FCSTD DOCUMENT  (FreeCAD 0.22R35720 (Git))
Label: DigitalTwin
License: All rights reserved
LicenseURL: http://en.wikipedia.org/wiki/All_rights_reserved
objects: Part::Feature×86, App::FeaturePython×76, App::Part×61, Part::FeaturePython×47, App::DocumentObjectGroup×4, Spreadsheet::Sheet×2
note: 132 computed .brp shape members not serialized (recipe doc carries the construction recipe); baked Part::Feature solids carry a one-line shape summary decoded from their .brp

FEATURE [Spreadsheet::Sheet] Spreadsheet  label="Offsets"
  cells = C3='Offsets; D4='R1; H4='R2; C5='Axis; D5='Y; E5='Z; F5='C; H5='Y; I5='Z; J5='C; C6='x; D6(R1_Y_x)=-404.5; E6(R1_Z_x)=-405; F6(R1_C_x)=-307.3; H6(R2_Y_x)=404.5; I6(R2_Z_x)=405; J6(R2_C_x)=307.3; C7='y; D7(R1_Y_y)=-285.5; E7(R1_Z_y)=-84.5; F7(R1_C_y)=-137.5; H7(R2_Y_y)=286.5; I7(R2_Z_y)=85.5; J7(R2_C_y)=138.5; C8='z; D8(R1_Y_z)=157; E8(R1_Z_z)=43; F8(R1_C_z)=207; H8(R2_Y_z)=157; I8(R2_Z_z)=43; J8(R2_C_z)=207; C9='Rot; C10='x; D10(R1_Y_rotX)=0; E10(R1_Z_rotX)=1; F10(R1_C_rotX)=0.58; H10(R2_Y_rotX)=0; I10(R2_Z_rotX)=0; J10(R2_C_rotX)=-0.58; C11='y; D11(R1_Y_rotY)=0; E11(R1_Z_rotY)=0; F11(R1_C_rotY)=0.58; H11(R2_Y_rotY)=0; I11(R2_Z_rotY)=0.71; J11(R2_C_rotY)=0.58; C12='z; D12(R1_Y_rotZ)=1; E12(R1_Z_rotZ)=0; F12(R1_C_rotZ)=-0.58; H12(R2_Y_rotZ)=-1; I12(R2_Z_rotZ)=0.71; J12(R2_C_rotZ)=-0.58; C13='a; D13(R1_Y_rotA)=90; E13(R1_Z_rotA)=90; F13(R1_C_rotA)=240; H13(R2_Y_rotA)=90; I13(R2_Z_rotA)=180; J13(R2_C_rotA)=120
FEATURE [Part::Feature] Part__Feature  label="SOLID"
  shape: bbox 125.9 x 42 x 74 mm, 165 faces (baked)
FEATURE [App::Part] Cartesian1_XYCarriage
  Group = -> [Part__Feature]
  Origin = -> Origin
  Placement = pos=(0,0,0) rot=(0.57735,0.57735,-0.57735;4.18879rad)
FEATURE [Part::Feature] Part__Feature002  label="SOLID001"
  shape: bbox 40 x 48 x 60 mm, 15 faces (baked)
FEATURE [App::Part] Cartesian1_BallNut
  Group = -> [Part__Feature002]
  Origin = -> Origin001
  Placement = pos=(-70,50,-1.84331e-08) rot=(0.707107,0,0.707107;3.14159rad)
FEATURE [App::Part] Carriage  label="C"
  Group = -> [Cartesian1_XYCarriage,Cartesian1_BallNut]
  Origin = -> Origin002
FEATURE [Part::Feature] Part__Feature028  label="SOLID002"
  shape: bbox 45 x 70.5 x 201 mm, 88 faces (baked)
FEATURE [App::Part] XMotorMount
  Group = -> [Part__Feature028]
  Origin = -> Origin003
  Placement = pos=(0,40,-6.39e-14) rot=(0,1,0;3.14159rad)
FEATURE [Part::Feature] Part__Feature030  label="SOLID003"
  shape: bbox 750 x 50 x 14 mm, 23 faces (baked)
FEATURE [App::Part] WS_10_40_X
  Group = -> [Part__Feature030]
  Origin = -> Origin004
  Placement = pos=(-45,20.5,69) rot=(0,0,1;0rad)
FEATURE [Part::Feature] Part__Feature032  label="SOLID004"
  shape: bbox 750 x 50 x 14 mm, 23 faces (baked)
FEATURE [App::Part] WS_10_40_X001
  Group = -> [Part__Feature032]
  Origin = -> Origin005
  Placement = pos=(-45,59.5,-69) rot=(1,0,0;3.14159rad)
FEATURE [Part::Feature] Part__Feature034  label="SOLID005"
  shape: bbox 45 x 70.5 x 201 mm, 82 faces (baked)
FEATURE [App::Part] XFloating
  Group = -> [Part__Feature034]
  Origin = -> Origin006
  Placement = pos=(512.817,40,-1.012e-13) rot=(0,0,1;0rad)
FEATURE [Part::Feature] Part__Feature036  label="Nema17 Stepper Motor"
  Placement = pos=(-85.5,39.998,-0.00196609) rot=(0,0,-1;1.5708rad)
  shape: bbox 64.02 x 42.26 x 48.39 mm, 313 faces (baked)
FEATURE [Part::Feature] Part__Feature037  label="SOLID006"
  shape: bbox 18.95 x 18.95 x 539 mm, 68 faces (baked)
FEATURE [App::Part] Cartesian1_BallScrew
  Group = -> [Part__Feature037]
  Origin = -> Origin007
  Placement = pos=(-9,40,-6.16e-14) rot=(0.64284,0.416548,0.64284;2.35221rad)
FEATURE [Part::Feature] Part__Feature039  label="SOLID007"
  shape: bbox 37 x 37 x 7 mm, 8 faces (baked)
FEATURE [App::Part] Cartesian2_BallBearing_25x37x7
  Group = -> [Part__Feature039]
  Origin = -> Origin008
  Placement = pos=(512.817,40,-1.012e-13) rot=(0.309507,0.899117,0.309507;1.67694rad)
FEATURE [Part::Feature] Part__Feature041  label="SOLID008"
  shape: bbox 25 x 25 x 32 mm, 12 faces (baked)
FEATURE [App::Part] Cartesian1_12_12_Clutch
  Group = -> [Part__Feature041]
  Origin = -> Origin009
  Placement = pos=(-31,40,-6.39e-14) rot=(0.684544,0.2506,0.684544;2.65051rad)
FEATURE [Part::Feature] Part__Feature043  label="SOLID009"
  shape: bbox 30 x 17 x 30 mm, 8 faces (baked)
FEATURE [App::Part] endCup
  Group = -> [Part__Feature043]
  Origin = -> Origin010
  Placement = pos=(512.817,40,-1.012e-13) rot=(0.652231,0.652231,-0.386251;2.4044rad)
FEATURE [Part::Feature] Part__Feature045  label="SOLID010"
  shape: bbox 8 x 18.5 x 18.2 mm, 16 faces (baked)
FEATURE [App::Part] Connector_female
  Group = -> [Part__Feature045]
  Origin = -> Origin011
  Placement = pos=(-32.15,60,39.85) rot=(0,-1,0;1.5708rad)
FEATURE [Part::Feature] Part__Feature047  label="SOLID011"
  shape: bbox 6.5 x 11 x 20 mm, 8 faces (baked)
FEATURE [App::Part] stopSw
  Group = -> [Part__Feature047]
  Origin = -> Origin012
  Placement = pos=(517.817,59,-40) rot=(0.707107,-0.707107,0;3.14159rad)
FEATURE [App::Part] X
  Group = -> [XMotorMount,WS_10_40_X,WS_10_40_X001,XFloating,Part__Feature036,Cartesian1_BallScrew,Cartesian2_BallBearing_25x37x7,Cartesian1_12_12_Clutch,endCup,Connector_female,stopSw]
  Origin = -> Origin013
FEATURE [Part::Feature] Part__Feature169  label="SOLID012"
  shape: bbox 74 x 74 x 26.9 mm, 46 faces (baked)
FEATURE [App::Part] YItemEnd
  Group = -> [Part__Feature169]
  Origin = -> Origin014
  Placement = pos=(0,0,7.1e-15) rot=(-1,0,0;1.5708rad)
FEATURE [Part::Feature] Part__Feature171  label="SOLID013"
  shape: bbox 74 x 100 x 44 mm, 108 faces (baked)
FEATURE [App::Part] YRodMount
  Group = -> [Part__Feature171]
  Origin = -> Origin015
  Placement = pos=(3.91e-14,-2,-74) rot=(1,0,0;1.5708rad)
FEATURE [Part::Feature] Part__Feature173  label="SOLID014"
  shape: bbox 69 x 75 x 42 mm, 58 faces (baked)
FEATURE [App::Part] YMotorMount
  Group = -> [Part__Feature173]
  Origin = -> Origin016
  Placement = pos=(2.41e-14,-6,-74) rot=(1,0,0;1.5708rad)
FEATURE [Part::Feature] Part__Feature175  label="SOLID015"
  shape: bbox 11 x 75 x 5 mm, 15 faces (baked)
FEATURE [App::Part] YEndStopMount
  Group = -> [Part__Feature175]
  Origin = -> Origin017
  Placement = pos=(64.39,-10,-37) rot=(1,0,0;1.5708rad)
FEATURE [Part::Feature] Part__Feature177  label="SOLID016"
  shape: bbox 6.5 x 11 x 20 mm, 8 faces (baked)
FEATURE [App::Part] stopSw001
  Group = -> [Part__Feature177]
  Origin = -> Origin018
  Placement = pos=(68.64,-15,-56.5) rot=(0,0,-1;1.5708rad)
FEATURE [App::Part] YSub1
  Group = -> [YItemEnd,YRodMount,YMotorMount,YEndStopMount,stopSw001]
  Origin = -> Origin019
  Placement = pos=(5.6488e-12,-70.2,36.5) rot=(0,0,1;0rad)
FEATURE [Part::Feature] Part__Feature179  label="SOLID017"
  shape: bbox 74 x 75 x 43.5 mm, 64 faces (baked)
FEATURE [App::Part] YFloatingMount
  Group = -> [Part__Feature179]
  Origin = -> Origin020
  Placement = pos=(11.243,57.3809,-132.972) rot=(0,0,1;0rad)
FEATURE [Part::Feature] Part__Feature181  label="SOLID018"
  shape: bbox 74 x 100 x 44 mm, 108 faces (baked)
FEATURE [App::Part] YRodMount001
  Group = -> [Part__Feature181]
  Origin = -> Origin021
  Placement = pos=(11.243,57.3809,-136.972) rot=(0,0,1;0rad)
FEATURE [App::Part] YSub2
  Group = -> [YFloatingMount,YRodMount001]
  Origin = -> Origin022
  Placement = pos=(486.757,-209.172,-94.3809) rot=(1,0,0;1.5708rad)
FEATURE [Part::Feature] Part__Feature183  label="SOLID019"
  shape: bbox 74 x 74 x 26.9 mm, 46 faces (baked)
FEATURE [App::Part] YItemEnd001
  Group = -> [Part__Feature183]
  Origin = -> Origin023
  Placement = pos=(572,-70.2,-37.5) rot=(0,0.707107,0.707107;3.14159rad)
FEATURE [Part::Feature] Part__Feature185  label="item_0037003_Profile_5_20x20_L=564_1"
  Placement = pos=(286,-55,-16.5) rot=(0,0,1;1.5708rad)
  shape: bbox 564 x 20 x 20 mm, 75 faces (baked)
FEATURE [Part::Feature] Part__Feature186  label="item_0037003_Profile_5_20x20_L=564_002"
  Placement = pos=(286,-55,15.5) rot=(0,0,1;1.5708rad)
  shape: bbox 564 x 20 x 20 mm, 75 faces (baked)
FEATURE [Part::Feature] Part__Feature187  label="SOLID020"
  shape: bbox 12 x 12 x 564 mm, 5 faces (baked)
FEATURE [App::Part] Cartesian1_12mm_Rod
  Group = -> [Part__Feature187]
  Origin = -> Origin024
  Placement = pos=(4,-97.2,-50.5) rot=(-0.52942,0.662894,-0.52942;1.97082rad)
FEATURE [Part::Feature] Part__Feature189  label="SOLID021"
  shape: bbox 12 x 12 x 564 mm, 5 faces (baked)
FEATURE [App::Part] Cartesian1_12mm_Rod001
  Group = -> [Part__Feature189]
  Origin = -> Origin025
  Placement = pos=(4,-97.2,50) rot=(0.611639,0.501791,0.611639;2.21143rad)
FEATURE [Part::Feature] Part__Feature191  label="SOLID022"
  shape: bbox 37 x 37 x 7 mm, 8 faces (baked)
FEATURE [App::Part] Cartesian2_BallBearing_25x37x7001
  Group = -> [Part__Feature191]
  Origin = -> Origin026
  Placement = pos=(564,-97.2,-1.37e-14) rot=(0.634829,0.440435,0.634829;2.31185rad)
FEATURE [Part::Feature] Part__Feature193  label="SOLID023"
  shape: bbox 34 x 9 x 45 mm, 26 faces (baked)
FEATURE [App::Part] Cartesian1_X_RodCover
  Group = -> [Part__Feature193]
  Origin = -> Origin027
  Placement = pos=(573.8,-97.2,-50) rot=(-0.57735,-0.57735,0.57735;2.0944rad)
FEATURE [Part::Feature] Part__Feature195  label="SOLID024"
  shape: bbox 34 x 9 x 45 mm, 26 faces (baked)
FEATURE [App::Part] Cartesian1_X_RodCover001
  Group = -> [Part__Feature195]
  Origin = -> Origin028
  Placement = pos=(573.8,-97.2,50) rot=(0.57735,-0.57735,-0.57735;2.0944rad)
FEATURE [Part::Feature] Part__Feature197  label="SOLID025"
  shape: bbox 34 x 9 x 45 mm, 26 faces (baked)
FEATURE [App::Part] Cartesian1_X_RodCover002
  Group = -> [Part__Feature197]
  Origin = -> Origin029
  Placement = pos=(24,-97.2,49.5) rot=(0.57735,0.57735,0.57735;2.0944rad)
FEATURE [Part::Feature] Part__Feature199  label="SOLID026"
  shape: bbox 34 x 9 x 45 mm, 26 faces (baked)
FEATURE [App::Part] Cartesian1_X_RodCover003
  Group = -> [Part__Feature199]
  Origin = -> Origin030
  Placement = pos=(24,-97.2,-50.5) rot=(0.57735,-0.57735,0.57735;4.18879rad)
FEATURE [Part::Feature] Part__Feature201  label="Nema17 Stepper Motor001"
  Placement = pos=(-40.5,-97.2,-5.58e-13) rot=(-0.57735,-0.57735,-0.57735;2.0944rad)
  shape: bbox 64.02 x 48.39 x 42.26 mm, 313 faces (baked)
FEATURE [Part::Feature] Part__Feature202  label="SOLID027"
  shape: bbox 25 x 25 x 32 mm, 12 faces (baked)
FEATURE [App::Part] Cartesian1_12_12_Clutch001
  Group = -> [Part__Feature202]
  Origin = -> Origin031
  Placement = pos=(7.85,-97.2,-5.127e-13) rot=(0.704181,-0.09087,0.704181;3.32283rad)
FEATURE [Part::Feature] Part__Feature204  label="SOLID028"
  shape: bbox 18.95 x 18.95 x 539 mm, 68 faces (baked)
FEATURE [App::Part] Cartesian1_BallScrew001
  Group = -> [Part__Feature204]
  Origin = -> Origin032
  Placement = pos=(29.85,-97.2,-4.874e-13) rot=(0.707075,-0.00955,0.707075;3.16069rad)
FEATURE [Part::Feature] Part__Feature206  label="SOLID029"
  shape: bbox 18 x 74 x 74 mm, 62 faces (baked)
FEATURE [App::Part] YItemEndCover
  Group = -> [Part__Feature206]
  Origin = -> Origin033
  Placement = pos=(535,-45.2,-0.5) rot=(0.57735,0.57735,0.57735;2.0944rad)
FEATURE [Part::Feature] Part__Feature208  label="SOLID030"
  shape: bbox 48 x 100 x 73 mm, 95 faces (baked)
FEATURE [App::Part] YCarriage
  Group = -> [Part__Feature208]
  Origin = -> Origin034
  Placement = pos=(201,0,-0.5) rot=(-0.57735,0.57735,0.57735;4.18879rad)
FEATURE [Part::Feature] Part__Feature210  label="SOLID031"
  shape: bbox 48 x 48 x 35 mm, 12 faces (baked)
FEATURE [App::Part] YCarriageNut
  Group = -> [Part__Feature210]
  Origin = -> Origin035
  Placement = pos=(201,-21,31.5) rot=(0,0,1;3.66519rad)
FEATURE [Part::Feature] Part__Feature212  label="WJ200UM_01_10_1"
  Placement = pos=(181,9,20.5) rot=(1,0,0;1.5708rad)
  shape: bbox 26 x 16.5 x 29 mm, 220 faces (baked)
FEATURE [Part::Feature] Part__Feature213  label="WJ200UM_01_10_002"
  Placement = pos=(181,9,-50.5) rot=(1,0,0;1.5708rad)
  shape: bbox 26 x 16.5 x 29 mm, 220 faces (baked)
FEATURE [Part::Feature] Part__Feature214  label="WJ200UM_01_10_003"
  Placement = pos=(221,9,49.5) rot=(0,0.707107,-0.707107;3.14159rad)
  shape: bbox 26 x 16.5 x 29 mm, 220 faces (baked)
FEATURE [Part::Feature] Part__Feature215  label="WJ200UM_01_10_004"
  Placement = pos=(221,9,-21.5) rot=(0,0.707107,-0.707107;3.14159rad)
  shape: bbox 26 x 16.5 x 29 mm, 220 faces (baked)
FEATURE [Part::Feature] Part__Feature216  label="SOLID032"
  shape: bbox 18 x 74 x 74 mm, 70 faces (baked)
FEATURE [App::Part] YItemEndCoverConnector
  Group = -> [Part__Feature216]
  Origin = -> Origin036
  Placement = pos=(37,-45.2,-0.5) rot=(0.57735,0.57735,-0.57735;4.18879rad)
FEATURE [Part::Feature] Part__Feature218  label="SOLID033"
  shape: bbox 30 x 17 x 30 mm, 8 faces (baked)
FEATURE [App::Part] endCup001
  Group = -> [Part__Feature218]
  Origin = -> Origin037
  Placement = pos=(571,-97.2,-7.1e-15) rot=(0.707107,-0.707107,0;3.14159rad)
FEATURE [App::Part] Y
  Group = -> [YSub1,YSub2,YItemEnd001,Part__Feature185,Part__Feature186,Cartesian1_12mm_Rod,Cartesian1_12mm_Rod001,Cartesian2_BallBearing_25x37x7001,Cartesian1_X_RodCover,Cartesian1_X_RodCover001,Cartesian1_X_RodCover002,Cartesian1_X_RodCover003,Part__Feature201,Cartesian1_12_12_Clutch001,Cartesian1_BallScrew001,YItemEndCover,YCarriage,YCarriageNut,Part__Feature212,Part__Feature213,Part__Feature214,+3 more]
  Origin = -> Origin038
FEATURE [Part::Feature] Part__Feature448  label="WW_10_40_10_2"
  Placement = pos=(50,2.1e-14,-69) rot=(0,0,1;1.5708rad)
  shape: bbox 100 x 73 x 22.5 mm, 942 faces (baked)
FEATURE [Part::Feature] Part__Feature449  label="WW_10_40_10_003"
  Placement = pos=(50,1.14e-13,69) rot=(0.707107,-0.707107,0;3.14159rad)
  shape: bbox 100 x 73 x 22.5 mm, 942 faces (baked)
FEATURE [Part::Feature] Part__Feature450  label="SOLID034"
  shape: bbox 100 x 100 x 90 mm, 167 faces (baked)
FEATURE [App::Part] ZCarriage
  Group = -> [Part__Feature450]
  Origin = -> Origin039
  Placement = pos=(0,-36.5,0) rot=(0,0,1;0rad)
FEATURE [Part::Feature] Part__Feature452  label="SOLID035"
  shape: bbox 40 x 48 x 60 mm, 15 faces (baked)
FEATURE [App::Part] Cartesian1_BallNut001
  Group = -> [Part__Feature452]
  Origin = -> Origin040
  Placement = pos=(30,0,-3.76e-14) rot=(0.57735,-0.57735,-0.57735;2.0944rad)
FEATURE [Part::Feature] Part__Feature454  label="SOLID036"
  shape: bbox 37 x 37 x 7 mm, 8 faces (baked)
FEATURE [App::Part] Cartesian2_BallBearing_25x37x7002
  Group = -> [Part__Feature454]
  Origin = -> Origin041
  Placement = pos=(21.5,29.5,-8.6e-15) rot=(-0.254373,0.683847,0.683847;2.64341rad)
FEATURE [Part::Feature] Part__Feature456  label="SOLID037"
  shape: bbox 36 x 10.82 x 10.82 mm, 15 faces (baked)
FEATURE [App::Part] DIN_EN_ISO_4762___M6_x_30  label="DIN EN ISO 4762 - M6 x 30"
  Group = -> [Part__Feature456]
  Origin = -> Origin042
  Placement = pos=(43.5,30,32) rot=(0.606018,0.515251,0.606018;4.09314rad)
FEATURE [Part::Feature] Part__Feature458  label="SOLID038"
  shape: bbox 36 x 10.82 x 10.82 mm, 15 faces (baked)
FEATURE [App::Part] DIN_EN_ISO_4762___M6_x_30001  label="DIN EN ISO 4762 - M6 x 031"
  Group = -> [Part__Feature458]
  Origin = -> Origin043
  Placement = pos=(-43.5,30,-32) rot=(-0.62292,0.473224,0.62292;2.2576rad)
FEATURE [Part::Feature] Part__Feature460  label="SOLID039"
  shape: bbox 13.5 x 39 x 90 mm, 50 faces (baked)
FEATURE [App::Part] ZCarriageBackHolder
  Group = -> [Part__Feature460]
  Origin = -> Origin044
  Placement = pos=(-38,24.5,3.55e-14) rot=(0,0,1;0rad)
FEATURE [Part::Feature] Part__Feature462  label="SOLID040"
  shape: bbox 30 x 20 x 30 mm, 11 faces (baked)
FEATURE [App::Part] ZScrewEndCup
  Group = -> [Part__Feature462]
  Origin = -> Origin045
  Placement = pos=(21.5,21.5,-8.6e-15) rot=(0,-1,0;1.19727rad)
FEATURE [Part::Feature] Part__Feature464  label="SOLID041"
  shape: bbox 30 x 27 x 90 mm, 34 faces (baked)
FEATURE [App::Part] ZCarriageFrontHolder
  Group = -> [Part__Feature464]
  Origin = -> Origin046
  Placement = pos=(-17,36.5,-3.55e-14) rot=(0,0,1;0rad)
FEATURE [Part::Feature] Part__Feature466  label="SOLID042"
  shape: bbox 500 x 50 x 14 mm, 23 faces (baked)
FEATURE [App::Part] WS_10_40_Z
  Group = -> [Part__Feature466]
  Origin = -> Origin047
  Placement = pos=(-17.5,518.5,-19.5) rot=(0.57735,-0.57735,-0.57735;2.0944rad)
FEATURE [Part::Feature] Part__Feature468  label="item_0037003_Profile_5_20x20_L=564_003"
  Placement = pos=(-27.5,300.5,-15) rot=(0,0,1;0rad)
  shape: bbox 20 x 564 x 20 mm, 75 faces (baked)
FEATURE [Part::Feature] Part__Feature469  label="item_0037003_Profile_5_20x20_L=564_004"
  Placement = pos=(-27.5,300.5,15) rot=(0,0,1;0rad)
  shape: bbox 20 x 564 x 20 mm, 75 faces (baked)
FEATURE [Part::Feature] Part__Feature470  label="SOLID043"
  shape: bbox 66 x 79 x 103.5 mm, 58 faces (baked)
FEATURE [App::Part] ZTop
  Group = -> [Part__Feature470]
  Origin = -> Origin048
  Placement = pos=(-17.5,507.5,-2.3e-14) rot=(0,-1,0;1.5708rad)
FEATURE [Part::Feature] Part__Feature472  label="Nema17 Stepper Motor002"
  Placement = pos=(21.5,585,-1.7e-14) rot=(1,0,0;3.14159rad)
  shape: bbox 42.26 x 64.02 x 48.39 mm, 313 faces (baked)
FEATURE [Part::Feature] Part__Feature473  label="SOLID044"
  shape: bbox 25 x 25 x 32 mm, 12 faces (baked)
FEATURE [App::Part] Cartesian1_12_12_Clutch002
  Group = -> [Part__Feature473]
  Origin = -> Origin049
  Placement = pos=(21.5,502.5,9.6e-14) rot=(-0.692316,0.510244,0.510244;1.93049rad)
FEATURE [Part::Feature] Part__Feature475  label="SOLID045"
  shape: bbox 18.93 x 18.93 x 487.5 mm, 293 faces (baked)
FEATURE [App::Part] Cartesian1_TrapezoidalScrew
  Group = -> [Part__Feature475]
  Origin = -> Origin050
  Placement = pos=(21.5,26,-7.6e-15) rot=(-0.086253,0.704472,0.704472;2.96951rad)
FEATURE [Part::Feature] Part__Feature477  label="SOLID046"
  shape: bbox 50 x 20 x 30 mm, 26 faces (baked)
FEATURE [App::Part] ZItemMount
  Group = -> [Part__Feature477]
  Origin = -> Origin051
  Placement = pos=(-17.5,160.313,4.60866e-09) rot=(0,-1,0;1.5708rad)
FEATURE [Part::Feature] Part__Feature479  label="SOLID047"
  shape: bbox 50 x 20 x 30 mm, 26 faces (baked)
FEATURE [App::Part] ZItemMount001
  Group = -> [Part__Feature479]
  Origin = -> Origin052
  Placement = pos=(-17.5,307.799,1.44e-14) rot=(0,-1,0;1.5708rad)
FEATURE [Part::Feature] Part__Feature481  label="SOLID048"
  shape: bbox 6.5 x 11 x 20 mm, 8 faces (baked)
FEATURE [App::Part] stopSw002
  Group = -> [Part__Feature481]
  Origin = -> Origin053
  Placement = pos=(-6,59,-6e-15) rot=(0,0,1;0rad)
FEATURE [Part::Feature] Part__Feature483  label="SOLID049"
  shape: bbox 8 x 18.5 x 18.2 mm, 16 faces (baked)
FEATURE [App::Part] Connector_female001
  Group = -> [Part__Feature483]
  Origin = -> Origin054
  Placement = pos=(27.15,26,32.15) rot=(0,-1,0;1.5708rad)
FEATURE [Part::Feature] Part__Feature485  label="SOLID050"
  shape: bbox 45 x 9.2 x 9.2 mm, 15 faces (baked)
FEATURE [App::Part] DIN_EN_ISO_4762___M5_x_40  label="DIN EN ISO 4762 - M5 x 40"
  Group = -> [Part__Feature485]
  Origin = -> Origin055
  Placement = pos=(30,13.435,-13.435) rot=(0,-0.379283,0.925281;3.14159rad)
FEATURE [Part::Feature] Part__Feature487  label="SOLID051"
  shape: bbox 4.7 x 9.238 x 9.238 mm, 13 faces (baked)
FEATURE [App::Part] ISO_4032___M5___ISO  label="ISO 4032 - M5 - ISO"
  Group = -> [Part__Feature487]
  Origin = -> Origin056
  Placement = pos=(-9.7,13.435,-13.435) rot=(1,0,0;0.523599rad)
FEATURE [Part::Feature] Part__Feature489  label="SOLID052"
  shape: bbox 60 x 20 x 30 mm, 34 faces (baked)
FEATURE [App::Part] ZItemMountCable
  Group = -> [Part__Feature489]
  Origin = -> Origin057
  Placement = pos=(-17.5,454.911,0) rot=(0,-1,0;1.5708rad)
FEATURE [Part::Feature] Part__Feature491  label="SOLID053"
  shape: bbox 46 x 10 x 12.5 mm, 22 faces (baked)
FEATURE [App::Part] ZTopCable
  Group = -> [Part__Feature491]
  Origin = -> Origin058
  Placement = pos=(-52.5,515.5,-1.5e-14) rot=(0,-1,0;1.5708rad)
FEATURE [Part::Feature] Part__Feature493  label="SOLID054"
  shape: bbox 29 x 7.577 x 7.577 mm, 15 faces (baked)
FEATURE [App::Part] ISO_4762___M4_x_25ISO  label="ISO 4762 - M4 x 25ISO"
  Group = -> [Part__Feature493]
  Origin = -> Origin059
  Placement = pos=(-58.5,515.5,-15) rot=(0,0,1;0rad)
FEATURE [App::Part] Z
  Group = -> [Part__Feature448,Part__Feature449,ZCarriage,Cartesian1_BallNut001,Cartesian2_BallBearing_25x37x7002,DIN_EN_ISO_4762___M6_x_30,DIN_EN_ISO_4762___M6_x_30001,ZCarriageBackHolder,ZScrewEndCup,ZCarriageFrontHolder,WS_10_40_Z,Part__Feature468,Part__Feature469,ZTop,Part__Feature472,Cartesian1_12_12_Clutch002,Cartesian1_TrapezoidalScrew,ZItemMount,ZItemMount001,stopSw002,Connector_female001,+5 more]
  Origin = -> Origin060
FEATURE [App::DocumentObjectGroup] Group  label="Import"
  Group = -> [Carriage,X,Y,Z]
FEATURE [Part::Feature] Carriage001  label="CR1"
  Placement = pos=(-307.3,-137.5,207) rot=(-0.57735,-0.57735,0.57735;2.0944rad)
  shape: bbox 42 x 74 x 125.9 mm, 180 faces, 2 solids (baked)
FEATURE [Part::Feature] X001  label="XR1"
  Placement = pos=(57.8173,-84.5,3) rot=(0,0.707107,0.707107;3.14159rad)
  shape: bbox 790.5 x 201 x 78.52 mm, 649 faces, 11 solids (baked)
FEATURE [Part::Feature] Y001  label="YR1"
  Placement = pos=(-404.5,-285.5,157) rot=(0,0,1;1.5708rad)
  shape: bbox 136.2 x 612.5 x 118.5 mm, 2245 faces, 29 solids (baked)
FEATURE [Part::Feature] Z001  label="ZR1"
  Placement = pos=(-405,-84.5,43) rot=(1,0,0;1.5708rad)
  shape: bbox 113.5 x 135 x 623 mm, 3223 faces, 26 solids (baked)
FEATURE [Part::Feature] Part__Feature494  label="BR"
  Placement = pos=(0,0,0) rot=(1,0,0;1.5708rad)
  shape: bbox 1000 x 800 x 3 mm, 6 faces, 0 solids (baked)
FEATURE [Part::Feature] Carriage002  label="CR2"
  Placement = pos=(307.3,138.5,207) rot=(-0.57735,0.57735,-0.57735;2.0944rad)
  shape: bbox 42 x 74 x 125.9 mm, 180 faces, 2 solids (baked)
FEATURE [Part::Feature] X002  label="XR2"
  Placement = pos=(-57.8173,85.5,3) rot=(1,0,0;1.5708rad)
  shape: bbox 790.5 x 201 x 78.52 mm, 649 faces, 11 solids (baked)
FEATURE [Part::Feature] Y002  label="YR2"
  Placement = pos=(404.5,286.5,157) rot=(0,0,-1;1.5708rad)
  shape: bbox 136.2 x 612.5 x 118.5 mm, 2245 faces, 29 solids (baked)
FEATURE [Part::Feature] Z002  label="ZR2"
  Placement = pos=(405,85.5,43) rot=(0,0.707107,0.707107;3.14159rad)
  shape: bbox 113.5 x 135 x 623 mm, 3223 faces, 26 solids (baked)
FEATURE [Part::FeaturePython] Parts  label="Parts_R1"  # WARN: FeaturePython — macro-defined, semantics opaque (R4)
  Group = -> [Carriage001,X001,Y001,Z001,Part__Feature494,Carriage002,X002,Y002,Z002]
  GroupMode = 0
FEATURE [Part::Feature] Carriage003  label="R1_C"
  Placement = pos=(-307.3,-137.5,207) rot=(0.58,0.58,-0.58;4.18879rad)
  shape: bbox 42 x 74 x 125.9 mm, 180 faces, 2 solids (baked)
FEATURE [Part::Feature] X003  label="R1_X"
  Placement = pos=(57.8173,-84.5,3) rot=(0,0.707107,0.707107;3.14159rad)
  shape: bbox 790.5 x 201 x 78.52 mm, 649 faces, 11 solids (baked)
FEATURE [Part::Feature] Y003  label="R1_Y"
  Placement = pos=(-404.5,-285.5,157) rot=(0,0,1;1.5708rad)
  shape: bbox 136.2 x 612.5 x 118.5 mm, 2245 faces, 29 solids (baked)
FEATURE [Part::Feature] Z003  label="R1_Z"
  Placement = pos=(-405,-84.5,43) rot=(1,0,0;1.5708rad)
  shape: bbox 113.5 x 135 x 623 mm, 3223 faces, 26 solids (baked)
FEATURE [Part::Feature] Part__Feature495  label="B1"
  Placement = pos=(0,0,0) rot=(1,0,0;1.5708rad)
  shape: bbox 1000 x 800 x 3 mm, 6 faces, 0 solids (baked)
FEATURE [Spreadsheet::Sheet] Spreadsheet001  label="Ranges"
  cells = C4='[mm]; D4='[mm/rot]; E4='[steps/rot]; F4='stepping; G4='max steps; I4='v[steps/s]; B5='x; C5(Range_X_mm)=409; D5(Range_X_mmRot)=10; E5(Range_X_stepsRot)=200; F5(Range_X_stepping)=0.5; G5(Range_X_maxSteps)==C5 / D5 * E5 / F5; I5=400; B6='y; C6(Range_Y_mm)=350; D6(Range_Y_mmRot)=10; E6(Range_Y_stepsRot)=200; F6(Range_Y_stepping)==1 / 2; G6(Range_Y_maxSteps)==C6 / D6 * E6 / F6; I6=400; B7='z; C7(Range_Z_mm)=344; D7(Range_Z_mmRot)=4; E7(Range_Z_stepsRot)=200; F7(Range_Z_stepping)==1 / 2; G7(Range_Z_maxSteps)==C7 / D7 * E7 / F7; I7=1000
FEATURE [App::DocumentObjectGroup] Group003  label="Sheets"
  Group = -> [Spreadsheet,Spreadsheet001]
FEATURE [Part::Feature] Z004  label="R2_Z"
  Placement = pos=(405,85.5,43) rot=(0,0.707107,0.707107;3.14159rad)
  shape: bbox 113.5 x 135 x 623 mm, 3223 faces, 26 solids (baked)
FEATURE [Part::Feature] Y004  label="R2_Y"
  Placement = pos=(404.5,286.5,157) rot=(0,0,-1;1.5708rad)
  shape: bbox 136.2 x 612.5 x 118.5 mm, 2245 faces, 29 solids (baked)
FEATURE [Part::Feature] X004  label="R2_X"
  Placement = pos=(-57.8173,85.5,3) rot=(1,0,0;1.5708rad)
  shape: bbox 790.5 x 201 x 78.52 mm, 649 faces, 11 solids (baked)
FEATURE [Part::Feature] Carriage004  label="R2_C"
  Placement = pos=(307.3,138.5,207) rot=(0.57735,-0.57735,0.57735;4.18879rad)
  shape: bbox 42 x 74 x 125.9 mm, 180 faces, 2 solids (baked)
FEATURE [App::DocumentObjectGroup] Group002  label="Models"
  Group = -> [Carriage003,X003,Y003,Z003,Part__Feature495,Z004,Y004,X004,Carriage004]
FEATURE [App::DocumentObjectGroup] Group001  label="Assembly"
  Group = -> [Assembly]
FEATURE [Part::FeaturePython] Assembly  label="Robots"  # WARN: FeaturePython — macro-defined, semantics opaque (R4)
  AutoRelax = true
  BuildShape = 0
  Freeze = false
  Group = -> [Constraints,Elements,Parts]
  Verbose = false
  _SolverType = 1
  _Version = 1
FEATURE [App::FeaturePython] Constraints  label="Constraints_R1"  # WARN: FeaturePython — macro-defined, semantics opaque (R4)
  Group = -> [Constraint,Constraint001,Constraint002,Constraint003,Constraint004,Constraint005,Constraint006,Constraint007,Constraint008,Constraint009,Constraint010,Constraint011,Constraint012,Constraint013,Constraint014,Constraint015,Constraint016,Constraint017,Constraint018,Constraint019,Constraint020,Constraint021,Constraint022,Constraint023,Constraint024]
  _Version = 1
FEATURE [App::FeaturePython] Elements  label="Elements_R1"  # WARN: FeaturePython — macro-defined, semantics opaque (R4)
  Group = -> [_Element,_Element001,_Element002,_Element003,_Element004,_Element005,_Element006,_Element007,_Element008,_Element009,_Element010,_Element011,_Element012,_Element013,_Element014,_Element015,_Element016,_Element017,_Element018,_Element019,_Element020,_Element021,_Element022,_Element023,_Element024,_Element025,_Element026,_Element027,_Element028,_Element029,_Element030,_Element031,_Element032,+12 more]
FEATURE [App::FeaturePython] Constraint  label="Locked"  # WARN: FeaturePython — macro-defined, semantics opaque (R4)
  Disabled = false
  Group = -> [ElementLink]
  _ConstraintType = 0
  _Parent = -> Constraints
FEATURE [App::FeaturePython] ElementLink  label="_Element"  # link proxy (typed FeaturePython)
  LinkTransform = true
  LinkedObject = -> _Element
  _Parent = -> Constraint
FEATURE [Part::FeaturePython] _Element  # link proxy (typed FeaturePython)
  Detach = false
  LinkTransform = true
  LinkedObject = -> Part__Feature494 [Face5]
  _Parent = -> Elements
FEATURE [Part::FeaturePython] _Element001  # link proxy (typed FeaturePython)
  Detach = false
  LinkTransform = true
  LinkedObject = -> X001 [Face205]
  _Parent = -> Elements
FEATURE [App::FeaturePython] Constraint001  label="PlaneAlignment"  # WARN: FeaturePython — macro-defined, semantics opaque (R4)
  Angle = 0
  AnglePitch = 0
  AngleRoll = 0
  Cascade = false
  Disabled = false
  Group = -> [ElementLink001,ElementLink002]
  LockAngle = false
  _ConstraintType = 37
  _Parent = -> Constraints
FEATURE [App::FeaturePython] ElementLink001  label="_Element001"  # link proxy (typed FeaturePython)
  LinkTransform = true
  LinkedObject = -> _Element001
  _Parent = -> Constraint001
FEATURE [App::FeaturePython] ElementLink002  label="_Element"  # link proxy (typed FeaturePython)
  LinkTransform = true
  LinkedObject = -> _Element
  _Parent = -> Constraint001
FEATURE [App::FeaturePython] Constraint002  label="PlaneAlignment001"  # WARN: FeaturePython — macro-defined, semantics opaque (R4)
  Angle = 0
  AnglePitch = 0
  AngleRoll = 0
  Cascade = false
  Disabled = false
  Group = -> [ElementLink003,ElementLink004]
  LockAngle = false
  _ConstraintType = 37
  _Parent = -> Constraints
FEATURE [App::FeaturePython] ElementLink003  label="_Element002"  # link proxy (typed FeaturePython)
  LinkTransform = true
  LinkedObject = -> _Element002
  _Parent = -> Constraint002
FEATURE [Part::FeaturePython] _Element002  # link proxy (typed FeaturePython)
  Detach = false
  LinkTransform = true
  LinkedObject = -> X001 [Face215]
  _Parent = -> Elements
FEATURE [App::FeaturePython] ElementLink004  label="_Element003"  # link proxy (typed FeaturePython)
  LinkTransform = true
  LinkedObject = -> _Element003
  _Parent = -> Constraint002
FEATURE [Part::FeaturePython] _Element003  # link proxy (typed FeaturePython)
  Detach = false
  LinkTransform = true
  LinkedObject = -> Part__Feature494 [Face1]
  _Parent = -> Elements
FEATURE [App::FeaturePython] Constraint003  label="PlaneAlignment002"  # WARN: FeaturePython — macro-defined, semantics opaque (R4)
  Angle = 0
  AnglePitch = 0
  AngleRoll = 0
  Cascade = false
  Disabled = false
  Group = -> [ElementLink005,ElementLink006]
  LockAngle = false
  Offset = 215
  _ConstraintType = 37
  _Parent = -> Constraints
FEATURE [App::FeaturePython] ElementLink005  label="_Element004"  # link proxy (typed FeaturePython)
  LinkTransform = true
  LinkedObject = -> _Element004
  _Parent = -> Constraint003
FEATURE [Part::FeaturePython] _Element004  # link proxy (typed FeaturePython)
  Detach = false
  LinkTransform = true
  LinkedObject = -> X001 [Face81]
  _Parent = -> Elements
FEATURE [App::FeaturePython] ElementLink006  label="_Element005"  # link proxy (typed FeaturePython)
  LinkTransform = true
  LinkedObject = -> _Element005
  _Parent = -> Constraint003
FEATURE [Part::FeaturePython] _Element005  # link proxy (typed FeaturePython)
  Detach = false
  LinkTransform = true
  LinkedObject = -> Part__Feature494 [Face4]
  _Parent = -> Elements
FEATURE [App::FeaturePython] Constraint004  label="AxialAlignment"  # WARN: FeaturePython — macro-defined, semantics opaque (R4)
  Angle = 0
  AnglePitch = 0
  AngleRoll = 0
  Disabled = false
  Group = -> [ElementLink007,ElementLink008]
  LockAngle = false
  Multiply = false
  _ConstraintType = 36
  _Parent = -> Constraints
FEATURE [App::FeaturePython] ElementLink007  label="_Element006"  # link proxy (typed FeaturePython)
  LinkTransform = true
  LinkedObject = -> _Element006
  _Parent = -> Constraint004
FEATURE [Part::FeaturePython] _Element006  # link proxy (typed FeaturePython)
  Detach = false
  LinkTransform = true
  LinkedObject = -> Z001 [Face1851]
  _Parent = -> Elements
FEATURE [App::FeaturePython] ElementLink008  label="_Element007"  # link proxy (typed FeaturePython)
  LinkTransform = true
  LinkedObject = -> _Element007
  _Parent = -> Constraint004
FEATURE [Part::FeaturePython] _Element007  # link proxy (typed FeaturePython)
  Detach = false
  LinkTransform = true
  LinkedObject = -> X001 [Face126]
  _Parent = -> Elements
FEATURE [Part::FeaturePython] _Element008  # link proxy (typed FeaturePython)
  Detach = false
  LinkTransform = true
  LinkedObject = -> Z001 [Face1934]
  _Parent = -> Elements
FEATURE [App::FeaturePython] Constraint005  label="SameOrientation"  # WARN: FeaturePython — macro-defined, semantics opaque (R4)
  Disabled = false
  Group = -> [ElementLink009,ElementLink010]
  _ConstraintType = 2
  _Parent = -> Constraints
FEATURE [App::FeaturePython] ElementLink009  label="_Element008"  # link proxy (typed FeaturePython)
  LinkTransform = true
  LinkedObject = -> _Element008
  _Parent = -> Constraint005
FEATURE [App::FeaturePython] ElementLink010  label="_Element"  # link proxy (typed FeaturePython)
  LinkTransform = true
  LinkedObject = -> _Element
  _Parent = -> Constraint005
FEATURE [App::FeaturePython] Constraint006  label="AxialAlignment001"  # WARN: FeaturePython — macro-defined, semantics opaque (R4)
  Angle = 0
  AnglePitch = 0
  AngleRoll = 0
  Disabled = false
  Group = -> [ElementLink011,ElementLink012]
  LockAngle = false
  Multiply = false
  _ConstraintType = 36
  _Parent = -> Constraints
FEATURE [App::FeaturePython] ElementLink011  label="_Element009"  # link proxy (typed FeaturePython)
  LinkTransform = true
  LinkedObject = -> _Element009
  _Parent = -> Constraint006
FEATURE [Part::FeaturePython] _Element009  # link proxy (typed FeaturePython)
  Detach = false
  LinkTransform = true
  LinkedObject = -> Y001 [Face1728]
  _Parent = -> Elements
FEATURE [App::FeaturePython] ElementLink012  label="_Element010"  # link proxy (typed FeaturePython)
  LinkTransform = true
  LinkedObject = -> _Element010
  _Parent = -> Constraint006
FEATURE [Part::FeaturePython] _Element010  # link proxy (typed FeaturePython)
  Detach = false
  LinkTransform = true
  LinkedObject = -> Z001 [Face2203]
  _Parent = -> Elements
FEATURE [App::FeaturePython] Constraint007  label="SameOrientation001"  # WARN: FeaturePython — macro-defined, semantics opaque (R4)
  Disabled = false
  Group = -> [ElementLink013,ElementLink014]
  _ConstraintType = 2
  _Parent = -> Constraints
FEATURE [App::FeaturePython] ElementLink013  label="_Element011"  # link proxy (typed FeaturePython)
  LinkTransform = true
  LinkedObject = -> _Element011
  _Parent = -> Constraint007
FEATURE [Part::FeaturePython] _Element011  # link proxy (typed FeaturePython)
  Detach = false
  LinkTransform = true
  LinkedObject = -> Y001 [Face1229]
  _Parent = -> Elements
FEATURE [App::FeaturePython] ElementLink014  label="_Element012"  # link proxy (typed FeaturePython)
  LinkTransform = true
  LinkedObject = -> _Element012
  _Parent = -> Constraint007
FEATURE [Part::FeaturePython] _Element012  # link proxy (typed FeaturePython)
  Detach = false
  LinkTransform = true
  LinkedObject = -> Z001 [Face2380]
  _Parent = -> Elements
FEATURE [App::FeaturePython] Constraint008  label="PlaneAlignment003"  # WARN: FeaturePython — macro-defined, semantics opaque (R4)
  Angle = 0
  AnglePitch = 0
  AngleRoll = 0
  Cascade = false
  Disabled = false
  Group = -> [ElementLink015,ElementLink016]
  LockAngle = false
  _ConstraintType = 37
  _Parent = -> Constraints
FEATURE [App::FeaturePython] ElementLink015  label="_Element013"  # link proxy (typed FeaturePython)
  LinkTransform = true
  LinkedObject = -> _Element013
  _Parent = -> Constraint008
FEATURE [Part::FeaturePython] _Element013  # link proxy (typed FeaturePython)
  Detach = false
  LinkTransform = true
  LinkedObject = -> Z001 [Face2051]
  _Parent = -> Elements
FEATURE [App::FeaturePython] ElementLink016  label="_Element014"  # link proxy (typed FeaturePython)
  LinkTransform = true
  LinkedObject = -> _Element014
  _Parent = -> Constraint008
FEATURE [Part::FeaturePython] _Element014  # link proxy (typed FeaturePython)
  Detach = false
  LinkTransform = true
  LinkedObject = -> X001 [Face216]
  _Parent = -> Elements
FEATURE [App::FeaturePython] Constraint009  label="PlaneAlignment004"  # WARN: FeaturePython — macro-defined, semantics opaque (R4)
  Angle = 0
  AnglePitch = 0
  AngleRoll = 0
  Cascade = false
  Disabled = false
  Group = -> [ElementLink017,ElementLink018]
  LockAngle = false
  _ConstraintType = 37
  _Parent = -> Constraints
FEATURE [App::FeaturePython] ElementLink017  label="_Element015"  # link proxy (typed FeaturePython)
  LinkTransform = true
  LinkedObject = -> _Element015
  _Parent = -> Constraint009
FEATURE [Part::FeaturePython] _Element015  # link proxy (typed FeaturePython)
  Detach = false
  LinkTransform = true
  LinkedObject = -> Y001 [Face1275]
  _Parent = -> Elements
FEATURE [App::FeaturePython] ElementLink018  label="_Element016"  # link proxy (typed FeaturePython)
  LinkTransform = true
  LinkedObject = -> _Element016
  _Parent = -> Constraint009
FEATURE [Part::FeaturePython] _Element016  # link proxy (typed FeaturePython)
  Detach = false
  LinkTransform = true
  LinkedObject = -> Z001 [Face2172]
  _Parent = -> Elements
FEATURE [App::FeaturePython] Constraint010  label="AxialAlignment002"  # WARN: FeaturePython — macro-defined, semantics opaque (R4)
  Angle = 0
  AnglePitch = 0
  AngleRoll = 0
  Disabled = false
  Group = -> [ElementLink019,ElementLink020]
  LockAngle = false
  Multiply = false
  _ConstraintType = 36
  _Parent = -> Constraints
FEATURE [App::FeaturePython] ElementLink019  label="_Element017"  # link proxy (typed FeaturePython)
  LinkTransform = true
  LinkedObject = -> _Element017
  _Parent = -> Constraint010
FEATURE [Part::FeaturePython] _Element017  # link proxy (typed FeaturePython)
  Detach = false
  LinkTransform = true
  LinkedObject = -> Carriage001 [Face159]
  _Parent = -> Elements
FEATURE [App::FeaturePython] ElementLink020  label="_Element018"  # link proxy (typed FeaturePython)
  LinkTransform = true
  LinkedObject = -> _Element018
  _Parent = -> Constraint010
FEATURE [Part::FeaturePython] _Element018  # link proxy (typed FeaturePython)
  Detach = false
  LinkTransform = true
  LinkedObject = -> Y001 [Face610]
  _Parent = -> Elements
FEATURE [App::FeaturePython] Constraint011  label="Angle"  # WARN: FeaturePython — macro-defined, semantics opaque (R4)
  Angle = 180
  Disabled = false
  Group = -> [ElementLink021,ElementLink022]
  Supplement = false
  _ConstraintType = 27
  _Parent = -> Constraints
FEATURE [App::FeaturePython] ElementLink021  label="_Element019"  # link proxy (typed FeaturePython)
  LinkTransform = true
  LinkedObject = -> _Element019
  _Parent = -> Constraint011
FEATURE [Part::FeaturePython] _Element019  # link proxy (typed FeaturePython)
  Detach = false
  LinkTransform = true
  LinkedObject = -> Carriage001 [Face74]
  _Parent = -> Elements
FEATURE [App::FeaturePython] ElementLink022  label="_Element020"  # link proxy (typed FeaturePython)
  LinkTransform = true
  LinkedObject = -> _Element020
  _Parent = -> Constraint011
FEATURE [Part::FeaturePython] _Element020  # link proxy (typed FeaturePython)
  Detach = false
  LinkTransform = true
  LinkedObject = -> Y001 [Face242]
  _Parent = -> Elements
FEATURE [App::FeaturePython] Constraint012  label="PlaneAlignment005"  # WARN: FeaturePython — macro-defined, semantics opaque (R4)
  Angle = 0
  AnglePitch = 0
  AngleRoll = 0
  Cascade = false
  Disabled = false
  Group = -> [ElementLink023,ElementLink024]
  LockAngle = false
  _ConstraintType = 37
  _Parent = -> Constraints
FEATURE [App::FeaturePython] ElementLink023  label="_Element021"  # link proxy (typed FeaturePython)
  LinkTransform = true
  LinkedObject = -> _Element021
  _Parent = -> Constraint012
FEATURE [Part::FeaturePython] _Element021  # link proxy (typed FeaturePython)
  Detach = false
  LinkTransform = true
  LinkedObject = -> Carriage001 [Face120]
  _Parent = -> Elements
FEATURE [App::FeaturePython] ElementLink024  label="_Element022"  # link proxy (typed FeaturePython)
  LinkTransform = true
  LinkedObject = -> _Element022
  _Parent = -> Constraint012
FEATURE [Part::FeaturePython] _Element022  # link proxy (typed FeaturePython)
  Detach = false
  LinkTransform = true
  LinkedObject = -> Y001 [Face53]
  _Parent = -> Elements
FEATURE [App::FeaturePython] Constraint013  label="PlaneAlignment006"  # WARN: FeaturePython — macro-defined, semantics opaque (R4)
  Angle = 0
  AnglePitch = 0
  AngleRoll = 0
  Cascade = false
  Disabled = false
  Group = -> [ElementLink025,ElementLink026]
  LockAngle = false
  _ConstraintType = 37
  _Parent = -> Constraints
FEATURE [App::FeaturePython] ElementLink025  label="_Element023"  # link proxy (typed FeaturePython)
  LinkTransform = true
  LinkedObject = -> _Element023
  _Parent = -> Constraint013
FEATURE [Part::FeaturePython] _Element023  # link proxy (typed FeaturePython)
  Detach = false
  LinkTransform = true
  LinkedObject = -> X002 [Face215]
  _Parent = -> Elements
FEATURE [App::FeaturePython] ElementLink026  label="_Element024"  # link proxy (typed FeaturePython)
  LinkTransform = true
  LinkedObject = -> _Element024
  _Parent = -> Constraint013
FEATURE [Part::FeaturePython] _Element024  # link proxy (typed FeaturePython)
  Detach = false
  LinkTransform = true
  LinkedObject = -> Part__Feature494 [Face3]
  _Parent = -> Elements
FEATURE [App::FeaturePython] Constraint014  label="PlaneAlignment007"  # WARN: FeaturePython — macro-defined, semantics opaque (R4)
  Angle = 0
  AnglePitch = 0
  AngleRoll = 0
  Cascade = false
  Disabled = false
  Group = -> [ElementLink027,ElementLink028]
  LockAngle = false
  _ConstraintType = 37
  _Parent = -> Constraints
FEATURE [App::FeaturePython] ElementLink027  label="_Element025"  # link proxy (typed FeaturePython)
  LinkTransform = true
  LinkedObject = -> _Element025
  _Parent = -> Constraint014
FEATURE [Part::FeaturePython] _Element025  # link proxy (typed FeaturePython)
  Detach = false
  LinkTransform = true
  LinkedObject = -> X002 [Face205]
  _Parent = -> Elements
FEATURE [App::FeaturePython] ElementLink028  label="_Element"  # link proxy (typed FeaturePython)
  LinkTransform = true
  LinkedObject = -> _Element
  _Parent = -> Constraint014
FEATURE [App::FeaturePython] Constraint015  label="PlaneAlignment008"  # WARN: FeaturePython — macro-defined, semantics opaque (R4)
  Angle = 0
  AnglePitch = 0
  AngleRoll = 0
  Cascade = false
  Disabled = false
  Group = -> [ElementLink029,ElementLink030]
  LockAngle = false
  Offset = -31
  _ConstraintType = 37
  _Parent = -> Constraints
FEATURE [App::FeaturePython] ElementLink029  label="_Element026"  # link proxy (typed FeaturePython)
  LinkTransform = true
  LinkedObject = -> _Element026
  _Parent = -> Constraint015
FEATURE [Part::FeaturePython] _Element026  # link proxy (typed FeaturePython)
  Detach = false
  LinkTransform = true
  LinkedObject = -> X002 [Face79]
  _Parent = -> Elements
FEATURE [App::FeaturePython] ElementLink030  label="_Element027"  # link proxy (typed FeaturePython)
  LinkTransform = true
  LinkedObject = -> _Element027
  _Parent = -> Constraint015
FEATURE [Part::FeaturePython] _Element027  # link proxy (typed FeaturePython)
  Detach = false
  LinkTransform = true
  LinkedObject = -> X001 [Face79]
  _Parent = -> Elements
FEATURE [App::FeaturePython] Constraint016  label="AxialAlignment003"  # WARN: FeaturePython — macro-defined, semantics opaque (R4)
  Angle = 0
  AnglePitch = 0
  AngleRoll = 0
  Disabled = false
  Group = -> [ElementLink031,ElementLink032]
  LockAngle = false
  Multiply = false
  _ConstraintType = 36
  _Parent = -> Constraints
FEATURE [App::FeaturePython] ElementLink031  label="_Element028"  # link proxy (typed FeaturePython)
  LinkTransform = true
  LinkedObject = -> _Element028
  _Parent = -> Constraint016
FEATURE [Part::FeaturePython] _Element028  # link proxy (typed FeaturePython)
  Detach = false
  LinkTransform = true
  LinkedObject = -> Z002 [Face494]
  _Parent = -> Elements
FEATURE [App::FeaturePython] ElementLink032  label="_Element029"  # link proxy (typed FeaturePython)
  LinkTransform = true
  LinkedObject = -> _Element029
  _Parent = -> Constraint016
FEATURE [Part::FeaturePython] _Element029  # link proxy (typed FeaturePython)
  Detach = false
  LinkTransform = true
  LinkedObject = -> X002 [Face94]
  _Parent = -> Elements
FEATURE [App::FeaturePython] Constraint017  label="SameOrientation002"  # WARN: FeaturePython — macro-defined, semantics opaque (R4)
  Disabled = false
  Group = -> [ElementLink033,ElementLink034]
  _ConstraintType = 2
  _Parent = -> Constraints
FEATURE [App::FeaturePython] ElementLink033  label="_Element030"  # link proxy (typed FeaturePython)
  LinkTransform = true
  LinkedObject = -> _Element030
  _Parent = -> Constraint017
FEATURE [Part::FeaturePython] _Element030  # link proxy (typed FeaturePython)
  Detach = false
  LinkTransform = true
  LinkedObject = -> Z002 [Face2172]
  _Parent = -> Elements
FEATURE [App::FeaturePython] ElementLink034  label="_Element"  # link proxy (typed FeaturePython)
  LinkTransform = true
  LinkedObject = -> _Element
  _Parent = -> Constraint017
FEATURE [App::FeaturePython] Constraint018  label="PlaneAlignment009"  # WARN: FeaturePython — macro-defined, semantics opaque (R4)
  Angle = 0
  AnglePitch = 0
  AngleRoll = 0
  Cascade = false
  Disabled = false
  Group = -> [ElementLink035,ElementLink036]
  LockAngle = false
  _ConstraintType = 37
  _Parent = -> Constraints
FEATURE [App::FeaturePython] ElementLink035  label="_Element031"  # link proxy (typed FeaturePython)
  LinkTransform = true
  LinkedObject = -> _Element031
  _Parent = -> Constraint018
FEATURE [Part::FeaturePython] _Element031  # link proxy (typed FeaturePython)
  Detach = false
  LinkTransform = true
  LinkedObject = -> Z002 [Face2051]
  _Parent = -> Elements
FEATURE [App::FeaturePython] ElementLink036  label="_Element032"  # link proxy (typed FeaturePython)
  LinkTransform = true
  LinkedObject = -> _Element032
  _Parent = -> Constraint018
FEATURE [Part::FeaturePython] _Element032  # link proxy (typed FeaturePython)
  Detach = false
  LinkTransform = true
  LinkedObject = -> X002 [Face216]
  _Parent = -> Elements
FEATURE [App::FeaturePython] Constraint019  label="AxialAlignment004"  # WARN: FeaturePython — macro-defined, semantics opaque (R4)
  Angle = 0
  AnglePitch = 0
  AngleRoll = 0
  Disabled = false
  Group = -> [ElementLink037,ElementLink038]
  LockAngle = false
  Multiply = false
  _ConstraintType = 36
  _Parent = -> Constraints
FEATURE [App::FeaturePython] ElementLink037  label="_Element033"  # link proxy (typed FeaturePython)
  LinkTransform = true
  LinkedObject = -> _Element033
  _Parent = -> Constraint019
FEATURE [Part::FeaturePython] _Element033  # link proxy (typed FeaturePython)
  Detach = false
  LinkTransform = true
  LinkedObject = -> Y002 [Face1729]
  _Parent = -> Elements
FEATURE [App::FeaturePython] ElementLink038  label="_Element034"  # link proxy (typed FeaturePython)
  LinkTransform = true
  LinkedObject = -> _Element034
  _Parent = -> Constraint019
FEATURE [Part::FeaturePython] _Element034  # link proxy (typed FeaturePython)
  Detach = false
  LinkTransform = true
  LinkedObject = -> Z002 [Face2203]
  _Parent = -> Elements
FEATURE [App::FeaturePython] Constraint020  label="SameOrientation003"  # WARN: FeaturePython — macro-defined, semantics opaque (R4)
  Disabled = false
  Group = -> [ElementLink039,ElementLink040]
  _ConstraintType = 2
  _Parent = -> Constraints
FEATURE [App::FeaturePython] ElementLink039  label="_Element035"  # link proxy (typed FeaturePython)
  LinkTransform = true
  LinkedObject = -> _Element035
  _Parent = -> Constraint020
FEATURE [Part::FeaturePython] _Element035  # link proxy (typed FeaturePython)
  Detach = false
  LinkTransform = true
  LinkedObject = -> Y002 [Face1248]
  _Parent = -> Elements
FEATURE [App::FeaturePython] ElementLink040  label="_Element036"  # link proxy (typed FeaturePython)
  LinkTransform = true
  LinkedObject = -> _Element036
  _Parent = -> Constraint020
FEATURE [Part::FeaturePython] _Element036  # link proxy (typed FeaturePython)
  Detach = false
  LinkTransform = true
  LinkedObject = -> Z002 [Face2380]
  _Parent = -> Elements
FEATURE [App::FeaturePython] Constraint021  label="PlaneAlignment010"  # WARN: FeaturePython — macro-defined, semantics opaque (R4)
  Angle = 0
  AnglePitch = 0
  AngleRoll = 0
  Cascade = false
  Disabled = false
  Group = -> [ElementLink041,ElementLink042]
  LockAngle = false
  _ConstraintType = 37
  _Parent = -> Constraints
FEATURE [App::FeaturePython] ElementLink041  label="_Element037"  # link proxy (typed FeaturePython)
  LinkTransform = true
  LinkedObject = -> _Element037
  _Parent = -> Constraint021
FEATURE [Part::FeaturePython] _Element037  # link proxy (typed FeaturePython)
  Detach = false
  LinkTransform = true
  LinkedObject = -> Y002 [Face1275]
  _Parent = -> Elements
FEATURE [App::FeaturePython] ElementLink042  label="_Element030"  # link proxy (typed FeaturePython)
  LinkTransform = true
  LinkedObject = -> _Element030
  _Parent = -> Constraint021
FEATURE [App::FeaturePython] Constraint022  label="AxialAlignment005"  # WARN: FeaturePython — macro-defined, semantics opaque (R4)
  Angle = 0
  AnglePitch = 0
  AngleRoll = 0
  Disabled = false
  Group = -> [ElementLink043,ElementLink044]
  LockAngle = false
  Multiply = false
  _ConstraintType = 36
  _Parent = -> Constraints
FEATURE [App::FeaturePython] ElementLink043  label="_Element038"  # link proxy (typed FeaturePython)
  LinkTransform = true
  LinkedObject = -> _Element038
  _Parent = -> Constraint022
FEATURE [Part::FeaturePython] _Element038  # link proxy (typed FeaturePython)
  Detach = false
  LinkTransform = true
  LinkedObject = -> Carriage002 [Face159]
  _Parent = -> Elements
FEATURE [App::FeaturePython] ElementLink044  label="_Element039"  # link proxy (typed FeaturePython)
  LinkTransform = true
  LinkedObject = -> _Element039
  _Parent = -> Constraint022
FEATURE [Part::FeaturePython] _Element039  # link proxy (typed FeaturePython)
  Detach = false
  LinkTransform = true
  LinkedObject = -> Y002 [Face610]
  _Parent = -> Elements
FEATURE [Part::FeaturePython] _Element040  # link proxy (typed FeaturePython)
  Detach = false
  LinkTransform = true
  LinkedObject = -> Carriage002 [Face74]
  _Parent = -> Elements
FEATURE [Part::FeaturePython] _Element041  # link proxy (typed FeaturePython)
  Detach = false
  LinkTransform = true
  LinkedObject = -> Y002 [Face242]
  _Parent = -> Elements
FEATURE [Part::FeaturePython] _Element042  # link proxy (typed FeaturePython)
  Detach = false
  LinkTransform = true
  LinkedObject = -> Carriage002 [Face120]
  _Parent = -> Elements
FEATURE [Part::FeaturePython] _Element043  # link proxy (typed FeaturePython)
  Detach = false
  LinkTransform = true
  LinkedObject = -> Y002 [Face699]
  _Parent = -> Elements
FEATURE [Part::FeaturePython] _Element044  # link proxy (typed FeaturePython)
  Detach = false
  LinkTransform = true
  LinkedObject = -> Y002 [Face53]
  _Parent = -> Elements
FEATURE [App::FeaturePython] Constraint023  label="PointInPlane"  # WARN: FeaturePython — macro-defined, semantics opaque (R4)
  Disabled = false
  Group = -> [ElementLink045,ElementLink046]
  _ConstraintType = 3
  _Parent = -> Constraints
FEATURE [App::FeaturePython] ElementLink045  label="_Element042"  # link proxy (typed FeaturePython)
  LinkTransform = true
  LinkedObject = -> _Element042
  _Parent = -> Constraint023
FEATURE [App::FeaturePython] ElementLink046  label="_Element044"  # link proxy (typed FeaturePython)
  LinkTransform = true
  LinkedObject = -> _Element044
  _Parent = -> Constraint023
FEATURE [App::FeaturePython] Constraint024  label="Angle001"  # WARN: FeaturePython — macro-defined, semantics opaque (R4)
  Angle = 180
  Disabled = false
  Group = -> [ElementLink047,ElementLink048]
  Supplement = false
  _ConstraintType = 27
  _Parent = -> Constraints
FEATURE [App::FeaturePython] ElementLink047  label="_Element040"  # link proxy (typed FeaturePython)
  LinkTransform = true
  LinkedObject = -> _Element040
  _Parent = -> Constraint024
FEATURE [App::FeaturePython] ElementLink048  label="_Element041"  # link proxy (typed FeaturePython)
  LinkTransform = true
  LinkedObject = -> _Element041
  _Parent = -> Constraint024
